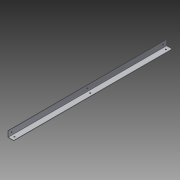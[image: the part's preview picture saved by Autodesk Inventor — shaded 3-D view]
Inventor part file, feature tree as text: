
AUTODESK INVENTOR PART (.ipt)
format: ipt  version: 2014 SP1 (Build 180222100, 222)  size: 100,864 bytes
history: native  units: in
note: dims shown in document units (in); Inventor stores cm internally (conversion verified against a paired STEP export)
features: extrude x3, sketch x3
ambient origin geometry x8: Origin, YZ Plane, XZ Plane, XY Plane, X Axis, Y Axis, Z Axis, Center Point
bodies: Solid1 (feature_tree)
feature tree (6):
  extrude  "Extrusion1"  Depth=0.0312in
  sketch  "Sketch2"  dims[d2=17.0in d3=0.0in d4=0.375in]
  sketch  "Sketch3"  dims[d5=0.125in d6=17.0in d7=1.1811in d9=8.125in d10=0.3937in d12=1.0in d14=0.125in d15=0.375in d16=17.0in d17=1.1811in d19=8.125in d20=0.3937in d22=1.0in d24=1.0in d25=0.0in d26=1.0in d27=0.0in]
  extrude  "Extrusion2"  Depth=17.0in
  extrude  "Extrusion3"  Depth=17.0in
  sketch  "Sketch1"  dims[d0=0.625in d1=0.0312in]
